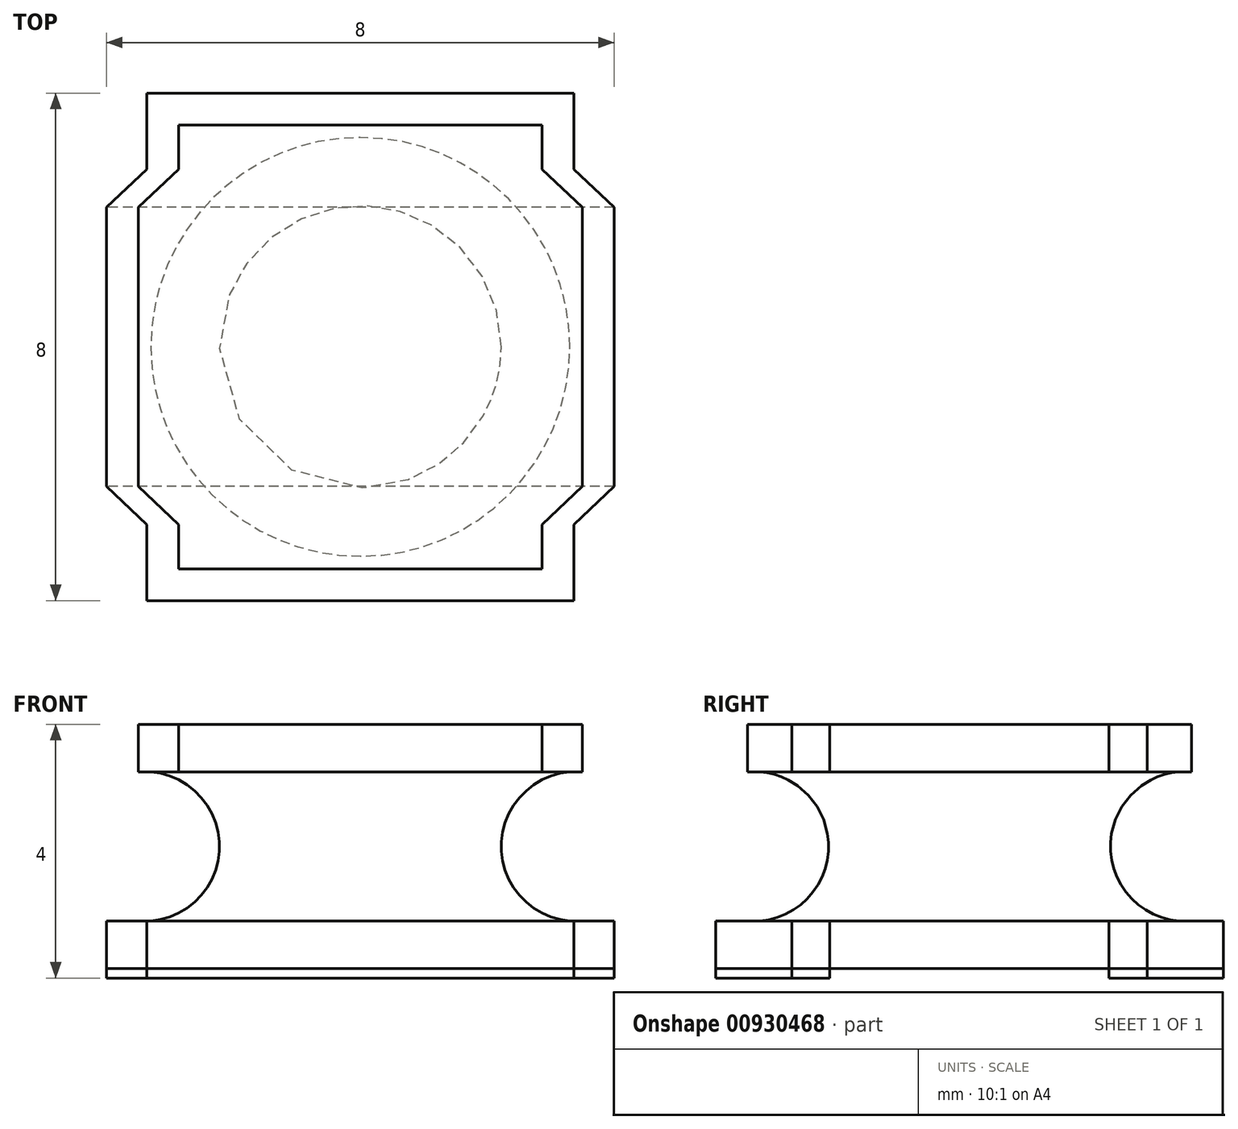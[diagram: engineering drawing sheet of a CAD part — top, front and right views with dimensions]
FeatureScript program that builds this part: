
annotation { "Feature Type Name" : "Feature", "Feature Type Description" : "" }
export const myFeature = defineFeature(function(context is Context, id is Id, definition is map)
    precondition{}
    {
        {
            var Q0;
            Q0=qCreatedBy(makeId("Top.planeOp"),FACE);
            var sketch = newSketch(context, id + "F0", { "sketchPlane" : qUnion([Q0])});
            skLineSegment(sketch, "E0.bottom", {"start": v(-4, 4) * mm, "end": v(4, 4) * mm});
            skLineSegment(sketch, "E0.top", {"start": v(-4, -4) * mm, "end": v(4, -4) * mm});
            skLineSegment(sketch, "E0.left", {"start": v(-4, 4) * mm, "end": v(-4, -4) * mm});
            skLineSegment(sketch, "E0.right", {"start": v(4, 4) * mm, "end": v(4, -4) * mm});
            skPoint(sketch, "E0.middle", {"position": v(0, 0) * mm});
            skLineSegment(sketch, "E1", {"start": v(4, 4) * mm, "end": v(4, 2.2) * mm});
            skLineSegment(sketch, "E2", {"start": v(4, 2.2) * mm, "end": v(-4, 2.2) * mm});
            skLineSegment(sketch, "E3.MirrorCS", {"start": v(4, -2.2) * mm, "end": v(-4, -2.2) * mm});
            skLineSegment(sketch, "E4", {"start": v(-4, 4) * mm, "end": v(-4, 2.8) * mm});
            skLineSegment(sketch, "E5", {"start": v(-4, 2.8) * mm, "end": v(4, 2.8) * mm});
            skLineSegment(sketch, "E6.MirrorCS", {"start": v(-4, -2.8) * mm, "end": v(4, -2.8) * mm});
            skLineSegment(sketch, "E7", {"start": v(-4, 2.2) * mm, "end": v(-3.36, 2.8) * mm});
            skLineSegment(sketch, "E8", {"start": v(-3.36, 2.8) * mm, "end": v(-3.36, 4) * mm});
            skLineSegment(sketch, "E9.MirrorCS", {"start": v(-4, -2.2) * mm, "end": v(-3.36, -2.8) * mm});
            skLineSegment(sketch, "E10.MirrorCS", {"start": v(-3.36, -2.8) * mm, "end": v(-3.36, -4) * mm});
            skLineSegment(sketch, "E11.MirrorCS", {"start": v(3.36, 2.8) * mm, "end": v(3.36, 4) * mm});
            skLineSegment(sketch, "E12.MirrorCS", {"start": v(4, 2.2) * mm, "end": v(3.36, 2.8) * mm});
            skLineSegment(sketch, "E13.MirrorCS", {"start": v(4, -2.2) * mm, "end": v(3.36, -2.8) * mm});
            skLineSegment(sketch, "E14.MirrorCS", {"start": v(3.36, -2.8) * mm, "end": v(3.36, -4) * mm});
            skSolve(sketch);
        }
        {
            var Q0;
            {var subQ0=sQuery(id+"F0.wireOp",EDGE,"E8");Q0=makeQuery(id+"F0.imprint","IMPRINT",FACE,{"disambiguationData":[TD([[makeQuery(id+"F0.imprint","IMPRINT",EDGE,{"derivedFrom":subQ0}),-1.0]])]});}
            var Q1;
            Q1=makeQuery(id+"F0.imprint","IMPRINT",FACE,{"disambiguationData":[TD([[makeQuery(id+"F0.imprint","IMPRINT",EDGE,{"derivedFrom":sQuery(id+"F0.wireOp",EDGE,"E2")}),-1.0]])]});
            var Q2;
            {var subQ0=sQuery(id+"F0.wireOp",EDGE,"E2");Q2=makeQuery(id+"F0.imprint","IMPRINT",FACE,{"disambiguationData":[TD([[makeQuery(id+"F0.imprint","IMPRINT",EDGE,{"derivedFrom":subQ0}),1.0]])]});}
            var Q3;
            Q3=makeQuery(id+"F0.imprint","IMPRINT",FACE,{"disambiguationData":[TD([[makeQuery(id+"F0.imprint","IMPRINT",EDGE,{"derivedFrom":sQuery(id+"F0.wireOp",EDGE,"E3.MirrorCS")}),1.0]])]});
            var Q4;
            {var subQ0=sQuery(id+"F0.wireOp",EDGE,"E10.MirrorCS");Q4=makeQuery(id+"F0.imprint","IMPRINT",FACE,{"disambiguationData":[TD([[makeQuery(id+"F0.imprint","IMPRINT",EDGE,{"derivedFrom":subQ0}),1.0]])]});}
            extrude(context, id + "F1", {"entities" : qUnion([Q0, Q1, Q2, Q3, Q4]), "depth" : 0.75 * mm, "offsetDistance" : 25 * mm});
        }
        {
            var Q0;
            Q0=makeQuery(id+"F1.opExtrude","SWEPT_BODY",BODY,{"disambiguationData":[OSD([sQuery(id+"F0.wireOp",EDGE,"E0.bottom"),sQuery(id+"F0.wireOp",EDGE,"E0.top"),sQuery(id+"F0.wireOp",EDGE,"E0.left"),sQuery(id+"F0.wireOp",EDGE,"E0.right"),sQuery(id+"F0.wireOp",EDGE,"E7"),sQuery(id+"F0.wireOp",EDGE,"E8"),sQuery(id+"F0.wireOp",EDGE,"E9.MirrorCS"),sQuery(id+"F0.wireOp",EDGE,"E10.MirrorCS"),sQuery(id+"F0.wireOp",EDGE,"E11.MirrorCS"),sQuery(id+"F0.wireOp",EDGE,"E12.MirrorCS"),sQuery(id+"F0.wireOp",EDGE,"E13.MirrorCS"),sQuery(id+"F0.wireOp",EDGE,"E14.MirrorCS")])]});
            transform(context, id + "F2", {"entities" : qUnion([Q0]), "transformType" : TransformType.TRANSLATION_3D, "dx" : 0 * mm, "dy" : 0 * mm, "dz" : 3.1 * mm, "makeCopy" : true});
        }
        {
            var Q0;
            Q0=qCreatedBy(makeId("Front.planeOp"),FACE);
            var sketch = newSketch(context, id + "F3", { "sketchPlane" : qUnion([Q0])});
            skLineSegment(sketch, "E15", {"start": v(0, 0) * mm, "end": v(3.5, 0) * mm});
            skLineSegment(sketch, "E16", {"start": v(3.5, 0) * mm, "end": v(3.5, 0.75) * mm});
            skLineSegment(sketch, "E17", {"start": v(3.5, 0.75) * mm, "end": v(3.5, 3.1) * mm});
            skArc(sketch, "E18", {"start": v(3.5, 3.1) * mm, "mid": v(2.22, 1.93) * mm, "end": v(3.5, 0.75) * mm});
            skLineSegment(sketch, "E19", {"start": v(3.5, 3.1) * mm, "end": v(0, 3.1) * mm});
            skLineSegment(sketch, "E20", {"start": v(0, 3.1) * mm, "end": v(0, 0.75) * mm});
            skLineSegment(sketch, "E21", {"start": v(0, 0.75) * mm, "end": v(3.5, 0.75) * mm});
            skSolve(sketch);
        }
        {
            var Q0;
            {var subQ5=sQuery(id+"F3.wireOp",EDGE,"E20");Q0=makeQuery(id+"F3.imprint","IMPRINT",FACE,{"disambiguationData":[TD([[makeQuery(id+"F3.imprint","IMPRINT",EDGE,{"derivedFrom":subQ5}),1.0]])]});}
            var Q1;
            Q1=sQuery(id+"F3.wireOp",EDGE,"E20");
            revolve(context, id + "F4", {"surfaceOperationType" : NewSurfaceOperationType.NEW, "entities" : qUnion([Q0]), "axis" : qUnion([Q1]), "revolveType" : RevolveType.FULL});
        }
        {
            var Q0;
            Q0=makeQuery(id+"F2.opPattern","COPY",FACE,{"derivedFrom":makeQuery(id+"F1.opExtrude","CAP_FACE",FACE,{"disambiguationData":[OSD([sQuery(id+"F0.wireOp",EDGE,"E0.bottom"),sQuery(id+"F0.wireOp",EDGE,"E0.top"),sQuery(id+"F0.wireOp",EDGE,"E0.left"),sQuery(id+"F0.wireOp",EDGE,"E0.right"),sQuery(id+"F0.wireOp",EDGE,"E7"),sQuery(id+"F0.wireOp",EDGE,"E8"),sQuery(id+"F0.wireOp",EDGE,"E9.MirrorCS"),sQuery(id+"F0.wireOp",EDGE,"E10.MirrorCS"),sQuery(id+"F0.wireOp",EDGE,"E11.MirrorCS"),sQuery(id+"F0.wireOp",EDGE,"E12.MirrorCS"),sQuery(id+"F0.wireOp",EDGE,"E13.MirrorCS"),sQuery(id+"F0.wireOp",EDGE,"E14.MirrorCS")])],"isStart":false}),"instanceName":"1"});
            var sketch = newSketch(context, id + "F5", { "sketchPlane" : qUnion([Q0])});
            skLineSegment(sketch, "E22", {"start": v(-3.36, 4) * mm, "end": v(-2.86, 4) * mm});
            skLineSegment(sketch, "E23", {"start": v(-2.86, 4) * mm, "end": v(-2.86, 3.5) * mm});
            skLineSegment(sketch, "E24", {"start": v(-2.86, 3.5) * mm, "end": v(-2.86, 2.8) * mm});
            skLineSegment(sketch, "E25", {"start": v(-2.86, 2.8) * mm, "end": v(-3.5, 2.2) * mm});
            skLineSegment(sketch, "E26", {"start": v(-3.5, 2.2) * mm, "end": v(-3.5, -2.2) * mm});
            skLineSegment(sketch, "E27", {"start": v(-3.5, -2.2) * mm, "end": v(-2.86, -2.8) * mm});
            skLineSegment(sketch, "E28", {"start": v(-2.86, -2.8) * mm, "end": v(-2.86, -3.5) * mm});
            skLineSegment(sketch, "E29", {"start": v(-2.86, -3.5) * mm, "end": v(0, -3.5) * mm});
            skLineSegment(sketch, "E30", {"start": v(-2.86, 3.5) * mm, "end": v(0, 3.5) * mm});
            skLineSegment(sketch, "E31.MirrorCS", {"start": v(2.86, -3.5) * mm, "end": v(0, -3.5) * mm});
            skLineSegment(sketch, "E32.MirrorCS", {"start": v(2.86, -2.8) * mm, "end": v(2.86, -3.5) * mm});
            skLineSegment(sketch, "E33.MirrorCS", {"start": v(3.5, -2.2) * mm, "end": v(2.86, -2.8) * mm});
            skLineSegment(sketch, "E34.MirrorCS", {"start": v(3.5, 2.2) * mm, "end": v(3.5, -2.2) * mm});
            skLineSegment(sketch, "E35.MirrorCS", {"start": v(2.86, 2.8) * mm, "end": v(3.5, 2.2) * mm});
            skLineSegment(sketch, "E36.MirrorCS", {"start": v(2.86, 3.5) * mm, "end": v(0, 3.5) * mm});
            skLineSegment(sketch, "E37.MirrorCS", {"start": v(2.86, 3.5) * mm, "end": v(2.86, 2.8) * mm});
            skSolve(sketch);
        }
        {
            var Q0;
            {var subQ2=sQuery(id+"F5.wireOp",EDGE,"E22");Q0=makeQuery(id+"F5.imprint","IMPRINT",FACE,{"disambiguationData":[TD([[makeQuery(id+"F5.imprint","IMPRINT",EDGE,{"derivedFrom":subQ2}),-1.0]])]});}
            extrude(context, id + "F6", {"entities" : qUnion([Q0]), "operationType" : NewBodyOperationType.REMOVE, "oppositeDirection" : true, "depth" : 0.75 * mm, "offsetDistance" : 25 * mm});
        }
        {
            var Q0;
            {var subQ0=sQuery(id+"F0.wireOp",EDGE,"E10.MirrorCS");Q0=makeQuery(id+"F0.imprint","IMPRINT",FACE,{"disambiguationData":[TD([[makeQuery(id+"F0.imprint","IMPRINT",EDGE,{"derivedFrom":subQ0}),1.0]])]});}
            var Q1;
            Q1=makeQuery(id+"F0.imprint","IMPRINT",FACE,{"disambiguationData":[TD([[makeQuery(id+"F0.imprint","IMPRINT",EDGE,{"derivedFrom":sQuery(id+"F0.wireOp",EDGE,"E3.MirrorCS")}),1.0]])]});
            var Q2;
            Q2=makeQuery(id+"F0.imprint","IMPRINT",FACE,{"disambiguationData":[TD([[makeQuery(id+"F0.imprint","IMPRINT",EDGE,{"derivedFrom":sQuery(id+"F0.wireOp",EDGE,"E2")}),-1.0]])]});
            var Q3;
            {var subQ0=sQuery(id+"F0.wireOp",EDGE,"E8");Q3=makeQuery(id+"F0.imprint","IMPRINT",FACE,{"disambiguationData":[TD([[makeQuery(id+"F0.imprint","IMPRINT",EDGE,{"derivedFrom":subQ0}),-1.0]])]});}
            extrude(context, id + "F7", {"entities" : qUnion([Q0, Q1, Q2, Q3]), "oppositeDirection" : true, "depth" : 0.15 * mm, "offsetDistance" : 25 * mm});
        }
    });
